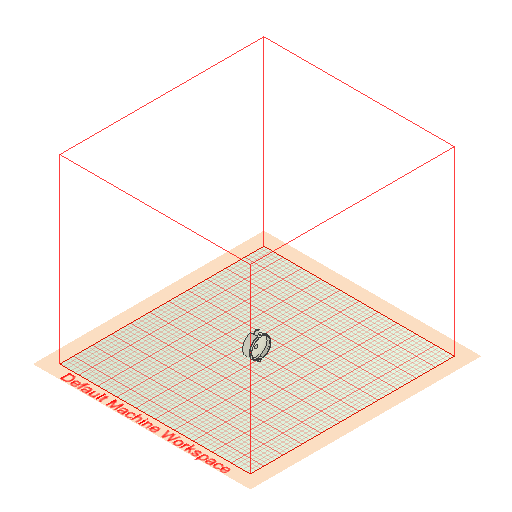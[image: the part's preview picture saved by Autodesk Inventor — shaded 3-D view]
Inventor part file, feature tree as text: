
AUTODESK INVENTOR PART (.ipt)
format: ipt  version: 2022.1 (Build 261234020, 234B)  size: 416,256 bytes
history: native  units: mm
features: extrude x12, sketch x7, fillet x1, other x1
ambient origin geometry x8: Origin, YZ Plane, XZ Plane, XY Plane, X Axis, Y Axis, Z Axis, Center Point
bodies: Solid1 (feature_tree)
feature tree (21):
  sketch  "Sketch1"  dims[d0=47.0mm d1=42.0mm]
  extrude  "Extrusion1"  Depth=42.0mm
  extrude  "Extrusion2"  Depth=10.0mm TaperAngle=0.0deg
  fillet  "Fillet1"  Radius=10.0mm
  extrude  "Extrusion3"  Depth=40.0mm TaperAngle=0.0deg
  extrude  "Extrusion4"  Depth=8.0mm
  extrude  "Extrusion5"  Depth=15.0mm
  extrude  "Extrusion6"  Depth=10.0mm TaperAngle=0.0deg
  extrude  "Extrusion7"  Depth=10.0mm TaperAngle=0.0deg
  other  "Lip1"
  extrude  "Extrusion8"  Depth=3.5mm
  extrude  "Extrusion9"  Depth=8.0mm
  sketch  "Sketch12"  dims[d14=10.0mm d15=0.0mm d16=15.0mm]
  sketch  "Sketch19"  dims[d17=100.0mm d18=0.0mm]
  extrude  "Extrusion28"  Depth=2.0mm
  extrude  "Extrusion29"  Depth=2.0mm
  extrude  "Extrusion30"  Depth=2.0mm
  sketch  "Sketch2"  dims[d2=100.0mm d3=0.0mm d4=95.0mm d5=0.0mm d6=10.0mm]
  sketch  "Sketch3"  dims[d7=50.0mm d8=0.0mm d9=40.0mm d10=0.0mm]
  sketch  "Sketch4"  dims[d11=1.0mm d12=0.0mm d13=8.0mm]
  sketch  "Sketch20"  dims[d19=3.0mm d20=1.3mm d21=0.0mm d22=0.0mm d23=0.872665mm d24=0.0mm d25=10.0mm d26=0.0mm d27=10.0mm d28=0.0mm d30=3.5mm d31=8.0mm d88=4.5mm d89=2.5mm d90=5.5mm d91=8.0mm d92=4.5mm d93=2.5mm d94=5.5mm d95=8.0mm d96=10.0mm d97=0.0mm d98=10.0mm d99=0.0mm d100=2.0mm d101=0.0mm d56=0.0mm d57=0.0mm d58=0.0mm d59=0.0mm d63=0.0mm d64=0.0mm d65=0.0mm d66=0.0mm d81=0.0mm d82=0.0mm d83=0.0mm d84=0.0mm d85=0.0mm d86=0.0mm]
